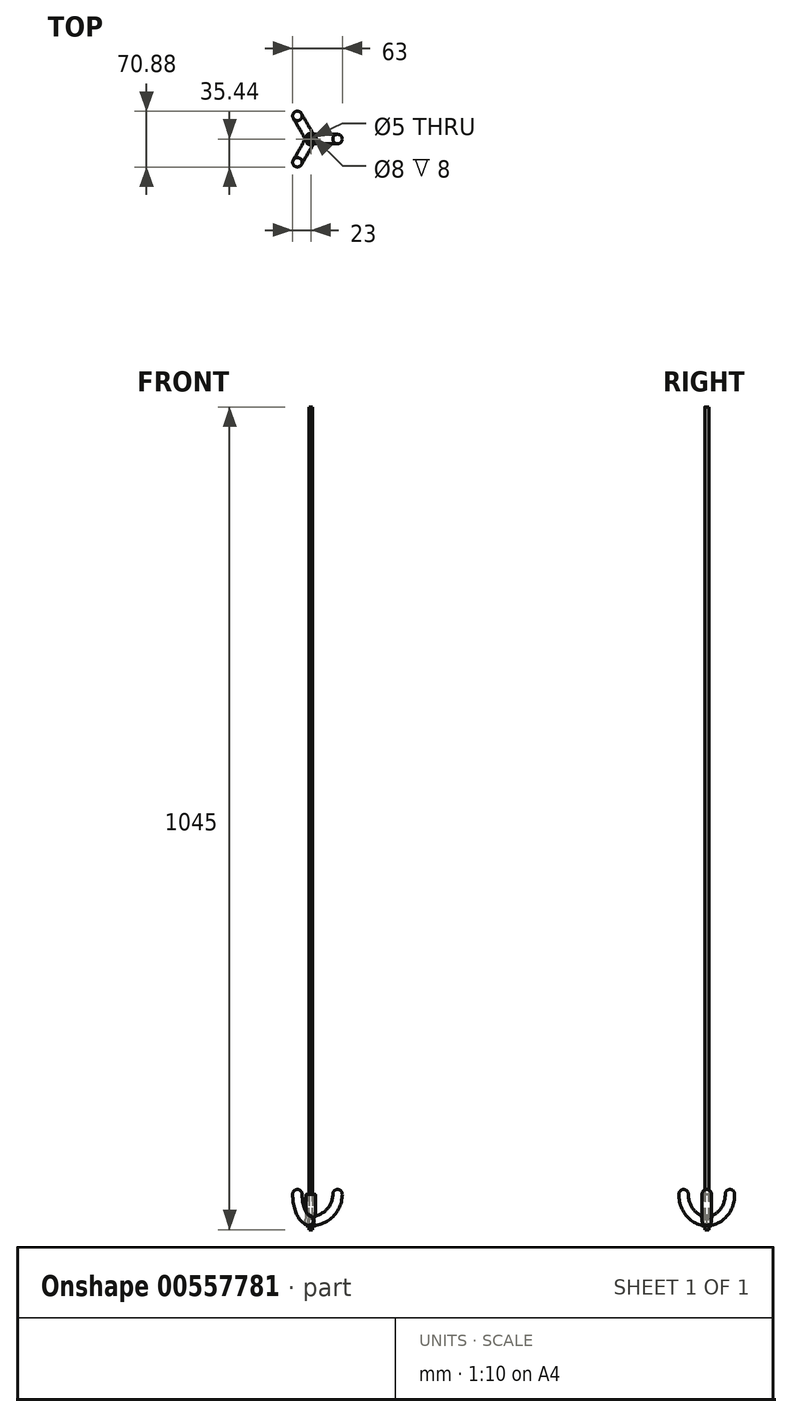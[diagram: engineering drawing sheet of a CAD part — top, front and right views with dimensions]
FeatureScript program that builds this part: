
annotation { "Feature Type Name" : "Feature", "Feature Type Description" : "" }
export const myFeature = defineFeature(function(context is Context, id is Id, definition is map)
    precondition{}
    {
        {
            var Q0;
            Q0=qCreatedBy(makeId("Front.planeOp"),FACE);
            var sketch = newSketch(context, id + "F0", { "sketchPlane" : qUnion([Q0])});
            skLineSegment(sketch, "E0", {"start": v(0, 0) * mm, "end": v(0, 6) * mm, "construction": true});
            skLineSegment(sketch, "E1", {"start": v(0, 0) * mm, "end": v(0, 40) * mm});
            skArc(sketch, "E2", {"start": v(0, 6) * mm, "mid": v(24.04, 15.96) * mm, "end": v(34, 40) * mm});
            skLineSegment(sketch, "E3", {"start": v(34, 40) * mm, "end": v(34, 46) * mm});
            skSolve(sketch);
        }
        {
            var Q0;
            Q0=qCreatedBy(makeId("Top.planeOp"),FACE);
            var Q1;
            Q1=sQuery(id+"F0.wireOp",VERTEX,"E2.start");
            cPlane(context, id + "F1", {"entities" : qUnion([Q0, Q1]), "cplaneType" : CPlaneType.PLANE_POINT, "offset" : 25 * mm, "width" : 150 * mm, "height" : 150 * mm});
        }
        {
            var Q0;
            Q0=qCreatedBy(id+"F1.planeOp",FACE);
            var sketch = newSketch(context, id + "F2", { "sketchPlane" : qUnion([Q0])});
            skCircle(sketch, "E4", {"center": v(0, 0) * mm, "radius": 6 * mm});
            skSolve(sketch);
        }
        {
            var Q0;
            Q0=qCreatedBy(makeId("Right.planeOp"),FACE);
            var sketch = newSketch(context, id + "F3", { "sketchPlane" : qUnion([Q0])});
            skCircle(sketch, "E5", {"center": v(0, 6) * mm, "radius": 6 * mm});
            skSolve(sketch);
        }
        {
            var Q0;
            Q0 = qSketchRegion(id + "F3", true);
            var Q1;
            Q1=sQuery(id+"F0.wireOp",EDGE,"E2");
            var Q2;
            Q2=sQuery(id+"F0.wireOp",EDGE,"E3");
            sweep(context, id + "F4", {"profiles" : qUnion([Q0]), "path" : qUnion([Q1, Q2])});
        }
        {
            var Q0;
            Q0=makeQuery(id+"F4.opSweep","CAP_EDGE",EDGE,{"disambiguationData":[OSD([sQuery(id+"F0.wireOp",VERTEX,"E2.end"),sQuery(id+"F3.wireOp",EDGE,"E5")])],"isStart":false});
            fillet(context, id + "F5", {"entities" : qUnion([Q0]), "radius" : 6 * mm, "tangentPropagation" : true, "allowEdgeOverflow" : false});
        }
        {
            var Q0;
            Q0=makeQuery(id+"F4.opSweep","SWEPT_BODY",BODY,{"disambiguationData":[OSD([sQuery(id+"F0.wireOp",EDGE,"E2"),sQuery(id+"F3.wireOp",EDGE,"E5")])]});
            var Q1;
            Q1=sQuery(id+"F0.wireOp",EDGE,"E1");
            circularPattern(context, id + "F6", {"operationType" : NewBodyOperationType.ADD, "entities" : qUnion([Q0]), "axis" : qUnion([Q1]), "angle" : 360 * degree, "instanceCount" : 3, "equalSpace" : true});
        }
        {
            var Q0;
            Q0=makeQuery(id+"F2.imprint","IMPRINT",FACE,{"disambiguationData":[TD([[makeQuery(id+"F2.imprint","IMPRINT",EDGE,{"derivedFrom":sQuery(id+"F2.wireOp",EDGE,"E4")}),1.0]])]});
            var Q1;
            Q1=sQuery(id+"F0.wireOp",EDGE,"E1");
            sweep(context, id + "F7", {"operationType" : NewBodyOperationType.ADD, "profiles" : qUnion([Q0]), "path" : qUnion([Q1])});
        }
        {
            var Q0;
            Q0=makeQuery(id+"F7.boolean.opBoolean","INTERSECT",EDGE,{"derivedFrom":[makeQuery(id+"F4.opSweep","SWEPT_FACE",FACE,{"disambiguationData":[OSD([sQuery(id+"F0.wireOp",EDGE,"E2"),sQuery(id+"F3.wireOp",EDGE,"E5")])]}),makeQuery(id+"F7.opSweep","SWEPT_FACE",FACE,{"disambiguationData":[OSD([sQuery(id+"F0.wireOp",EDGE,"E1"),sQuery(id+"F2.wireOp",EDGE,"E4")])]})]});
            var Q1;
            Q1=makeQuery(id+"F7.boolean.opBoolean","INTERSECT",EDGE,{"derivedFrom":[makeQuery(id+"F6.opPattern","COPY",FACE,{"derivedFrom":makeQuery(id+"F4.opSweep","SWEPT_FACE",FACE,{"disambiguationData":[OSD([sQuery(id+"F0.wireOp",EDGE,"E2"),sQuery(id+"F3.wireOp",EDGE,"E5")])]}),"instanceName":"2"}),makeQuery(id+"F7.opSweep","SWEPT_FACE",FACE,{"disambiguationData":[OSD([sQuery(id+"F0.wireOp",EDGE,"E1"),sQuery(id+"F2.wireOp",EDGE,"E4")])]})]});
            var Q2;
            Q2=makeQuery(id+"F7.boolean.opBoolean","INTERSECT",EDGE,{"derivedFrom":[makeQuery(id+"F6.opPattern","COPY",FACE,{"derivedFrom":makeQuery(id+"F4.opSweep","SWEPT_FACE",FACE,{"disambiguationData":[OSD([sQuery(id+"F0.wireOp",EDGE,"E2"),sQuery(id+"F3.wireOp",EDGE,"E5")])]}),"instanceName":"1"}),makeQuery(id+"F7.opSweep","SWEPT_FACE",FACE,{"disambiguationData":[OSD([sQuery(id+"F0.wireOp",EDGE,"E1"),sQuery(id+"F2.wireOp",EDGE,"E4")])]})]});
            var Q3;
            {var subQ0=makeQuery(id+"F4.opSweep","SWEPT_FACE",FACE,{"disambiguationData":[OSD([sQuery(id+"F0.wireOp",EDGE,"E2"),sQuery(id+"F3.wireOp",EDGE,"E5")])]});Q3=makeQuery(id+"F6.boolean.opBoolean","INTERSECT",EDGE,{"derivedFrom":[subQ0,makeQuery(id+"F6.opPattern","COPY",FACE,{"derivedFrom":subQ0,"instanceName":"1"})]});}
            var Q4;
            {var subQ0=makeQuery(id+"F4.opSweep","SWEPT_FACE",FACE,{"disambiguationData":[OSD([sQuery(id+"F0.wireOp",EDGE,"E2"),sQuery(id+"F3.wireOp",EDGE,"E5")])]});Q4=makeQuery(id+"F6.boolean.opBoolean","INTERSECT",EDGE,{"derivedFrom":[subQ0,makeQuery(id+"F6.opPattern","COPY",FACE,{"derivedFrom":subQ0,"instanceName":"2"})]});}
            var Q5;
            Q5=makeQuery(id+"F6.opPattern","COPY",FACE,{"derivedFrom":makeQuery(id+"F4.opSweep","SWEPT_FACE",FACE,{"disambiguationData":[OSD([sQuery(id+"F0.wireOp",EDGE,"E2"),sQuery(id+"F3.wireOp",EDGE,"E5")])]}),"instanceName":"1"});
            var Q6;
            {var subQ0=makeQuery(id+"F4.opSweep","SWEPT_FACE",FACE,{"disambiguationData":[OSD([sQuery(id+"F0.wireOp",EDGE,"E2"),sQuery(id+"F3.wireOp",EDGE,"E5")])]});Q6=makeQuery(id+"F6.boolean.opBoolean","INTERSECT",EDGE,{"derivedFrom":[makeQuery(id+"F6.opPattern","COPY",FACE,{"derivedFrom":subQ0,"instanceName":"1"}),makeQuery(id+"F6.opPattern","COPY",FACE,{"derivedFrom":subQ0,"instanceName":"2"})]});}
            fillet(context, id + "F8", {"entities" : qUnion([Q0, Q1, Q2, Q3, Q4, Q5, Q6]), "radius" : 1 * mm, "tangentPropagation" : true, "allowEdgeOverflow" : false});
        }
        {
            var Q0;
            Q0=makeQuery(id+"F7.opSweep","CAP_EDGE",EDGE,{"disambiguationData":[OSD([sQuery(id+"F0.wireOp",VERTEX,"E1.end"),sQuery(id+"F2.wireOp",EDGE,"E4")])],"isStart":false});
            fillet(context, id + "F9", {"entities" : qUnion([Q0]), "radius" : 1 * mm, "tangentPropagation" : true, "allowEdgeOverflow" : false});
        }
        {
            var Q0;
            Q0=makeQuery(id+"F7.opSweep","CAP_FACE",FACE,{"disambiguationData":[OSD([sQuery(id+"F0.wireOp",VERTEX,"E1.end"),sQuery(id+"F2.wireOp",EDGE,"E4")])],"isStart":false});
            var sketch = newSketch(context, id + "F10", { "sketchPlane" : qUnion([Q0])});
            skCircle(sketch, "E6", {"center": v(0, 0) * mm, "radius": 2.5 * mm});
            skSolve(sketch);
        }
        {
            var Q0;
            Q0=makeQuery(id+"F10.imprint","IMPRINT",FACE,{"disambiguationData":[TD([[makeQuery(id+"F10.imprint","IMPRINT",EDGE,{"derivedFrom":sQuery(id+"F10.wireOp",EDGE,"E6")}),1.0]])]});
            extrude(context, id + "F11", {"entities" : qUnion([Q0]), "operationType" : NewBodyOperationType.REMOVE, "endBound" : BoundingType.THROUGH_ALL, "oppositeDirection" : true, "depth" : 25 * mm, "offsetDistance" : 25 * mm});
        }
        {
            var Q0;
            Q0=qCreatedBy(makeId("Top.planeOp"),FACE);
            var sketch = newSketch(context, id + "F12", { "sketchPlane" : qUnion([Q0])});
            skCircle(sketch, "E7", {"center": v(0, 0) * mm, "radius": 4 * mm});
            skSolve(sketch);
        }
        {
            var Q0;
            Q0 = qSketchRegion(id + "F12", true);
            extrude(context, id + "F13", {"entities" : qUnion([Q0]), "operationType" : NewBodyOperationType.REMOVE, "depth" : 8 * mm, "offsetDistance" : 25 * mm});
        }
        {
            var Q0;
            Q0 = qSketchRegion(id + "F10", true);
            extrude(context, id + "F14", {"entities" : qUnion([Q0]), "depth" : 1000 * mm, "offsetDistance" : 25 * mm, "hasSecondDirection" : true, "secondDirectionOppositeDirection" : true, "secondDirectionDepth" : 45 * mm});
        }
    });
